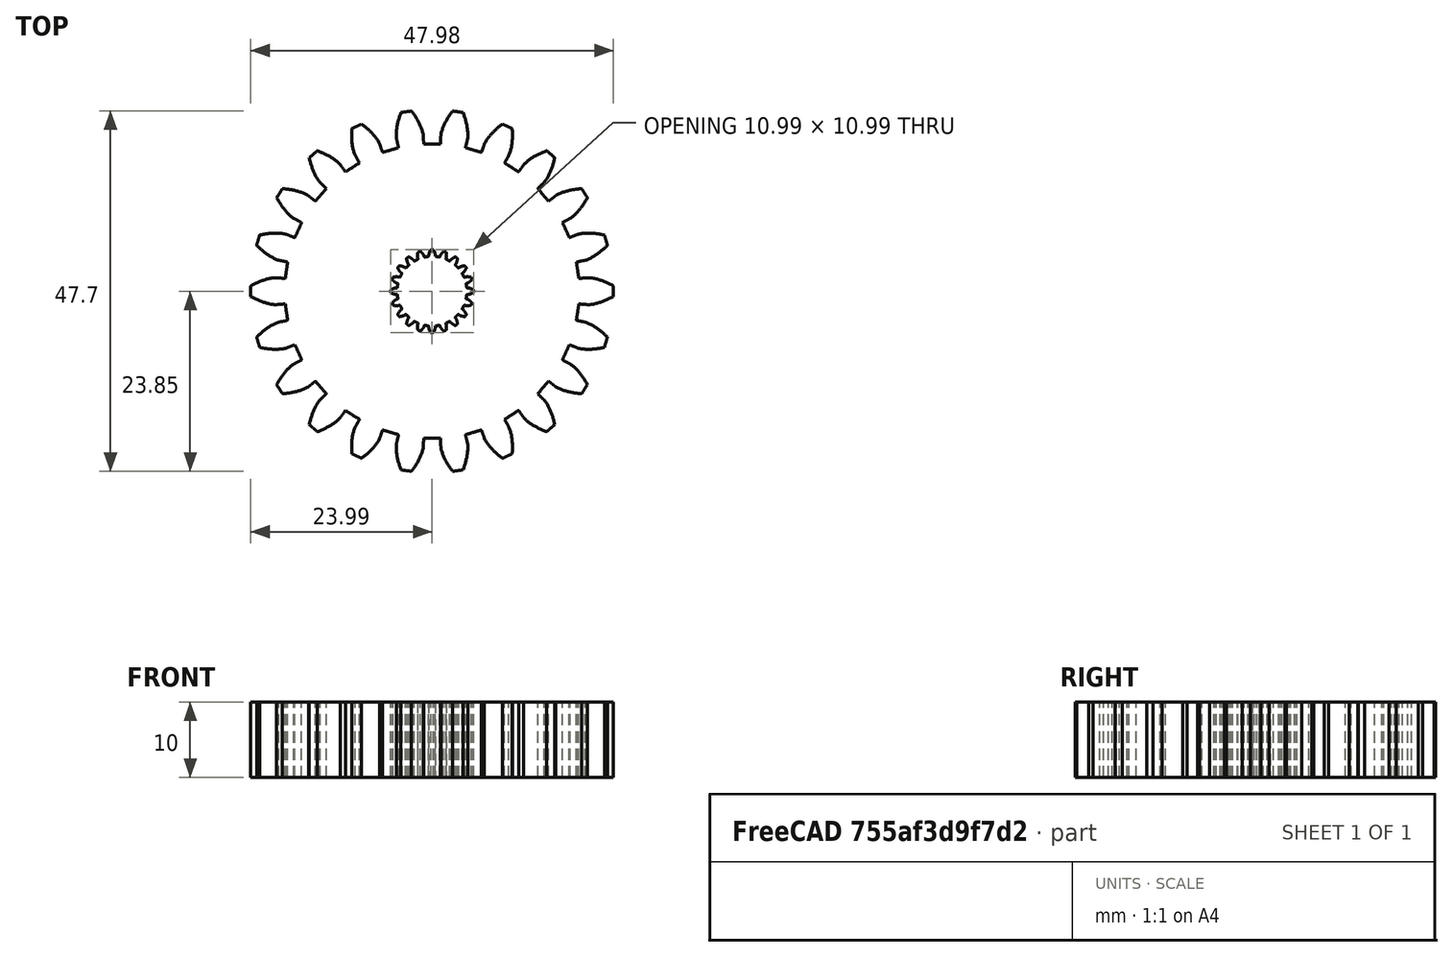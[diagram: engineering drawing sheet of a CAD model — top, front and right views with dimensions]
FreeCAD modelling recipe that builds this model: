
FCSTD DOCUMENT  (FreeCAD 0.17R13522 (Git))
Label: GearboxCouplingGear
License: All rights reserved
LicenseURL: http://en.wikipedia.org/wiki/All_rights_reserved
objects: Part::FeaturePython×2, PartDesign::Body×1, Part::Cut×1, App::Part×1
note: 4 computed .brp shape members not serialized (recipe doc carries the construction recipe); baked Part::Feature solids carry a one-line shape summary decoded from their .brp

FEATURE [PartDesign::Body] Body
  Origin = -> Origin001
FEATURE [Part::FeaturePython] InvoluteGear  # WARN: FeaturePython — macro-defined, semantics opaque (R4)
  backlash = 0
  beta = 0
  clearance = 0.25
  double_helix = false
  head = 0
  height = 10
  module = 2
  numpoints = 6
  pressure_angle = 20
  reversed_backlash = false
  shift = 0
  simple = false
  teeth = 22
  undercut = false
FEATURE [Part::FeaturePython] InvoluteGear001  # WARN: FeaturePython — macro-defined, semantics opaque (R4)
  backlash = 0
  beta = 0
  clearance = -0.25
  double_helix = false
  head = 0
  height = 10
  module = 0.5
  numpoints = 6
  pressure_angle = 20
  reversed_backlash = false
  shift = 0
  simple = false
  teeth = 20
  undercut = false
FEATURE [Part::Cut] Cut
  Base = -> InvoluteGear
  Tool = -> InvoluteGear001
FEATURE [App::Part] Part
  Group = -> [Body,InvoluteGear,InvoluteGear001,Cut]
  License = CC BY 3.0
  LicenseURL = http://creativecommons.org/licenses/by/3.0/
  Origin = -> Origin
